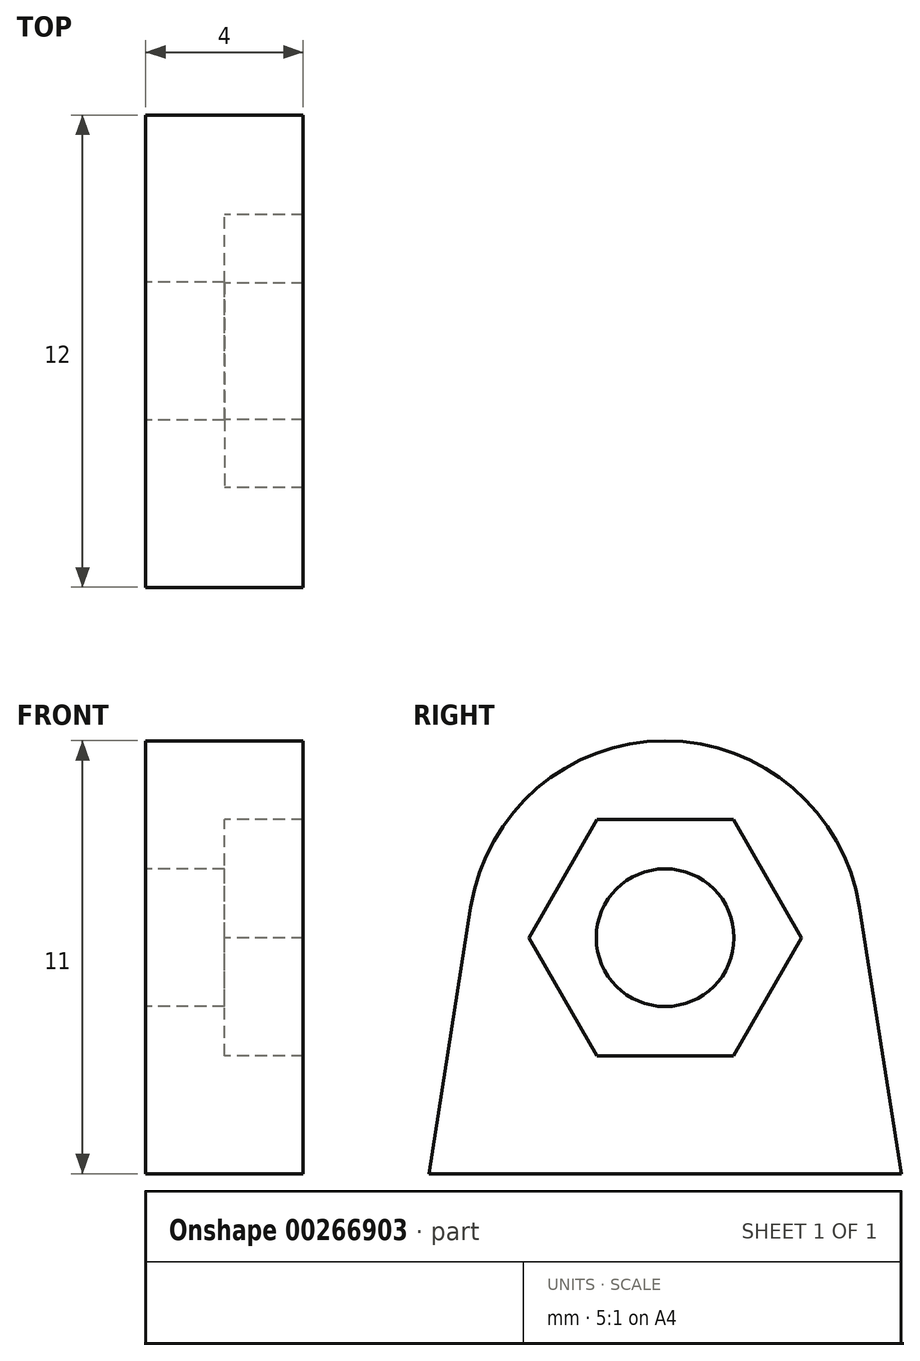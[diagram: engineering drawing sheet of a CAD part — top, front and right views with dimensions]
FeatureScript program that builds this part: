
annotation { "Feature Type Name" : "Feature", "Feature Type Description" : "" }
export const myFeature = defineFeature(function(context is Context, id is Id, definition is map)
    precondition{}
    {
        {
            var Q0;
            Q0=qCreatedBy(makeId("Right.planeOp"),FACE);
            var sketch = newSketch(context, id + "F0", { "sketchPlane" : qUnion([Q0])});
            skCircle(sketch, "E0", {"center": v(-26.65, 32.73) * mm, "radius": 5 * mm});
            skLineSegment(sketch, "E1", {"start": v(-32.65, 26.73) * mm, "end": v(-20.65, 26.73) * mm});
            skLineSegment(sketch, "E2", {"start": v(-31.6, 33.5) * mm, "end": v(-32.65, 26.73) * mm});
            skLineSegment(sketch, "E3", {"start": v(-21.71, 33.5) * mm, "end": v(-20.65, 26.73) * mm});
            skCircle(sketch, "E4", {"center": v(-26.65, 32.73) * mm, "radius": 1.75 * mm});
            skLineSegment(sketch, "E5.0", {"start": v(-30.12, 32.73) * mm, "end": v(-28.39, 35.73) * mm});
            skLineSegment(sketch, "E5.1", {"start": v(-28.39, 35.73) * mm, "end": v(-24.92, 35.73) * mm});
            skLineSegment(sketch, "E5.2", {"start": v(-24.92, 35.73) * mm, "end": v(-23.19, 32.73) * mm});
            skLineSegment(sketch, "E5.3", {"start": v(-23.19, 32.73) * mm, "end": v(-24.92, 29.73) * mm});
            skLineSegment(sketch, "E5.4", {"start": v(-24.92, 29.73) * mm, "end": v(-28.39, 29.73) * mm});
            skLineSegment(sketch, "E5.5", {"start": v(-28.39, 29.73) * mm, "end": v(-30.12, 32.73) * mm});
            skPoint(sketch, "E5.0.midPoint", {"position": v(-29.25, 34.23) * mm});
            skSolve(sketch);
        }
        {
            var Q0;
            Q0=makeQuery(id+"F0.imprint","IMPRINT",FACE,{"disambiguationData":[TD([[makeQuery(id+"F0.imprint","IMPRINT",EDGE,{"derivedFrom":sQuery(id+"F0.wireOp",EDGE,"E1")}),1.0]])]});
            var Q1;
            Q1=makeQuery(id+"F0.imprint","IMPRINT",FACE,{"disambiguationData":[TD([[makeQuery(id+"F0.imprint","IMPRINT",EDGE,{"derivedFrom":sQuery(id+"F0.wireOp",EDGE,"E5.0")}),1.0]])]});
            extrude(context, id + "F1", {"entities" : qUnion([Q0, Q1]), "depth" : 4 * mm});
        }
        {
            var Q0;
            Q0=makeQuery(id+"F0.imprint","IMPRINT",FACE,{"disambiguationData":[TD([[makeQuery(id+"F0.imprint","IMPRINT",EDGE,{"derivedFrom":sQuery(id+"F0.wireOp",EDGE,"E4")}),-1.0]])]});
            extrude(context, id + "F2", {"entities" : qUnion([Q0]), "operationType" : NewBodyOperationType.ADD, "depth" : 2 * mm});
        }
    });
